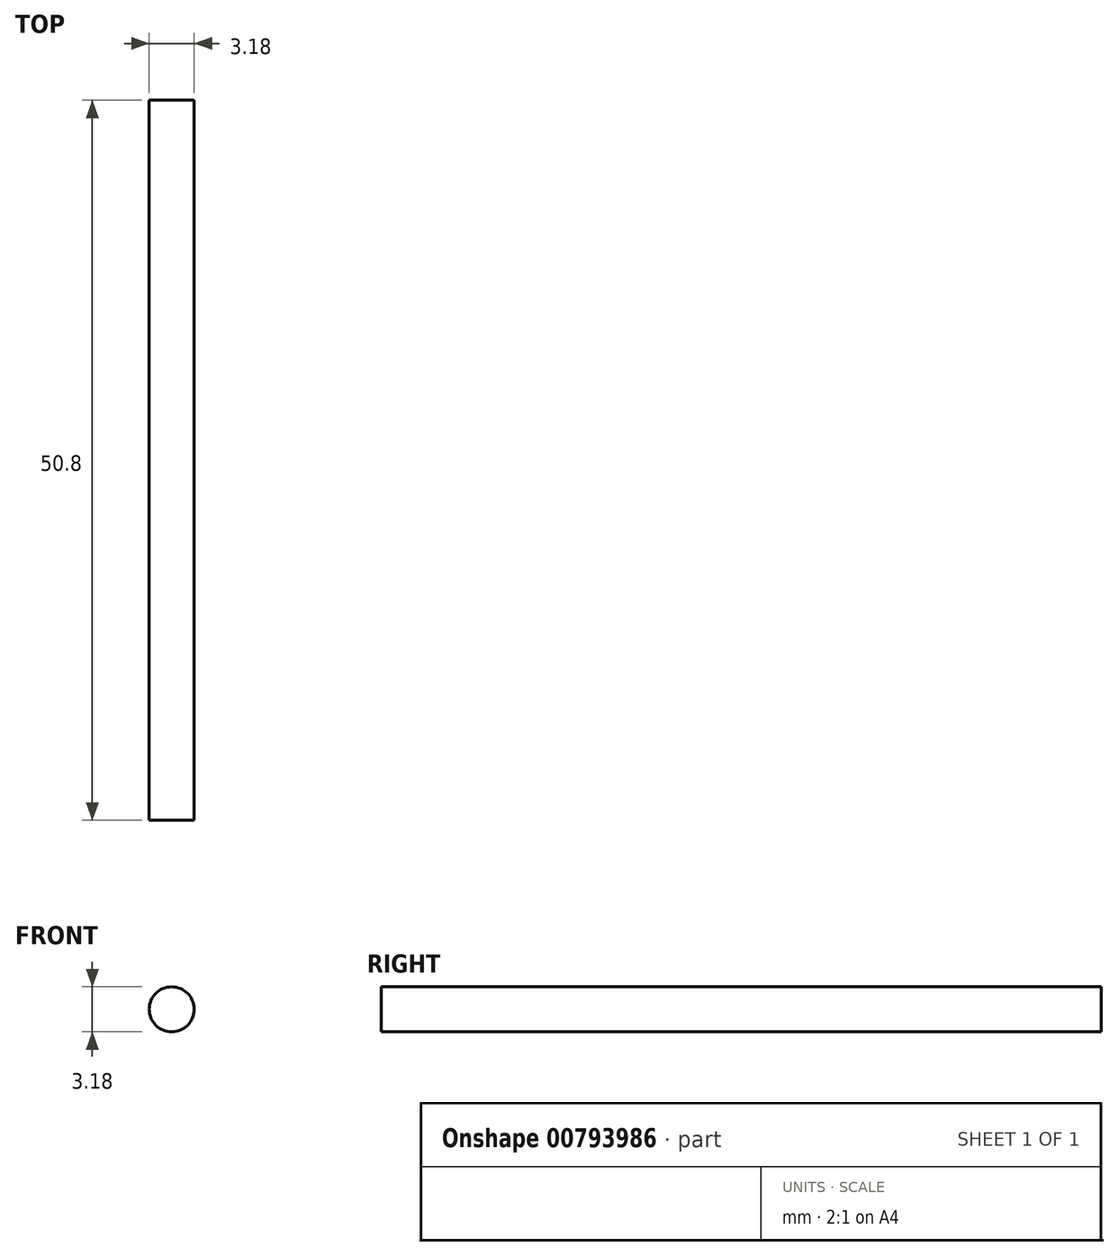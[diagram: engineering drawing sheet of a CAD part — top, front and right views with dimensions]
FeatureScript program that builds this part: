
annotation { "Feature Type Name" : "Feature", "Feature Type Description" : "" }
export const myFeature = defineFeature(function(context is Context, id is Id, definition is map)
    precondition{}
    {
        {
            var Q0;
            Q0=qCreatedBy(makeId("Front.planeOp"),FACE);
            var sketch = newSketch(context, id + "F0", { "sketchPlane" : qUnion([Q0])});
            skCircle(sketch, "E0", {"center": v(0, 0) * mm, "radius": 1.59 * mm});
            skSolve(sketch);
        }
        {
            var Q0;
            Q0 = qSketchRegion(id + "F0", true);
            extrude(context, id + "F1", {"entities" : qUnion([Q0]), "endBound" : BoundingType.SYMMETRIC, "depth" : 50.8 * mm, "offsetDistance" : 25.4 * mm});
        }
    });
